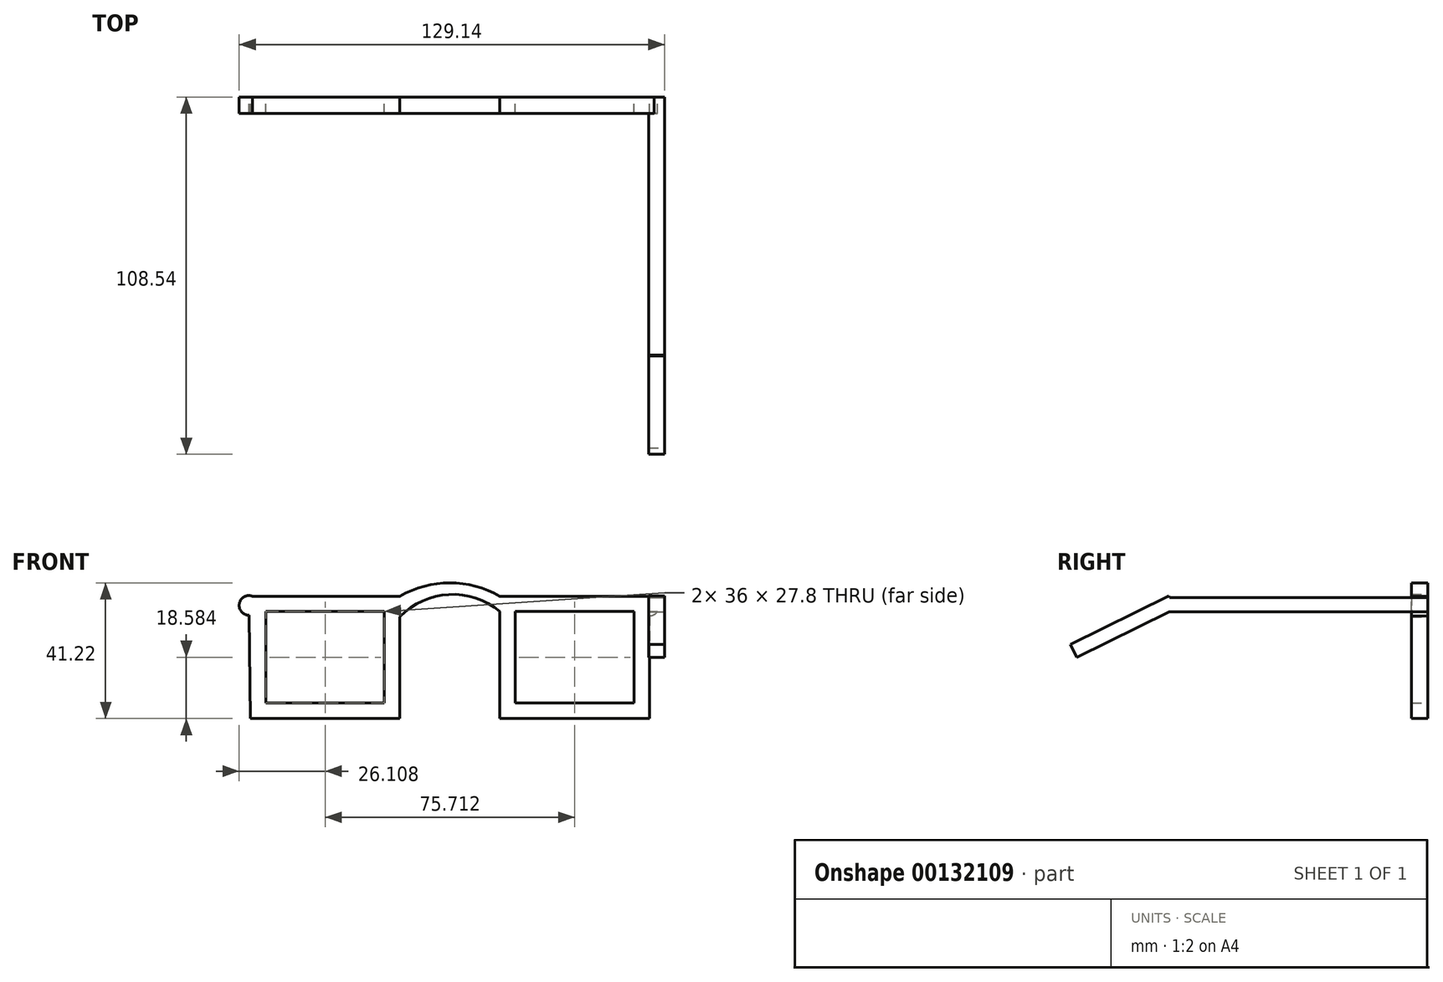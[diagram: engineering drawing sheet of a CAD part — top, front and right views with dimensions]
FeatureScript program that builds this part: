
annotation { "Feature Type Name" : "Feature", "Feature Type Description" : "" }
export const myFeature = defineFeature(function(context is Context, id is Id, definition is map)
    precondition{}
    {
        {
            var Q0;
            Q0=qCreatedBy(makeId("Front.planeOp"),FACE);
            var sketch = newSketch(context, id + "F0", { "sketchPlane" : qUnion([Q0])});
            skLineSegment(sketch, "E0.bottom", {"start": v(-75.72, 32.65) * mm, "end": v(-30.35, 32.65) * mm});
            skLineSegment(sketch, "E0.top", {"start": v(-75.72, -4.5) * mm, "end": v(-30.35, -4.5) * mm});
            skLineSegment(sketch, "E0.right", {"start": v(-30.35, 26.4) * mm, "end": v(-30.35, -4.5) * mm});
            skPoint(sketch, "E0.middle", {"position": v(-53.03, 14.07) * mm});
            skLineSegment(sketch, "E1.bottom", {"start": v(-71.03, 27.97) * mm, "end": v(-35.03, 27.97) * mm});
            skLineSegment(sketch, "E1.top", {"start": v(-71.03, 0.17) * mm, "end": v(-35.03, 0.17) * mm});
            skLineSegment(sketch, "E1.left", {"start": v(-71.03, 27.97) * mm, "end": v(-71.03, 0.17) * mm});
            skLineSegment(sketch, "E1.right", {"start": v(-35.03, 27.97) * mm, "end": v(-35.03, 0.17) * mm});
            skArc(sketch, "E2", {"start": v(-75.13, 32.65) * mm, "mid": v(-79.1, 30.37) * mm, "end": v(-76.16, 26.86) * mm});
            skLineSegment(sketch, "E3.trimOffspring", {"start": v(-76.16, 26.86) * mm, "end": v(-75.72, -4.5) * mm});
            skArc(sketch, "E4", {"start": v(0, 32.65) * mm, "mid": v(-15.17, 36.71) * mm, "end": v(-30.35, 32.65) * mm});
            skArc(sketch, "E5", {"start": v(0, 27.97) * mm, "mid": v(-15.48, 33.16) * mm, "end": v(-30.35, 26.4) * mm});
            skLineSegment(sketch, "E6.bottom", {"start": v(4.68, 27.97) * mm, "end": v(40.68, 27.97) * mm});
            skLineSegment(sketch, "E6.top", {"start": v(4.68, 0.17) * mm, "end": v(40.68, 0.17) * mm});
            skLineSegment(sketch, "E6.left", {"start": v(4.68, 27.97) * mm, "end": v(4.68, 0.17) * mm});
            skLineSegment(sketch, "E6.right", {"start": v(40.68, 27.97) * mm, "end": v(40.68, 0.17) * mm});
            skPoint(sketch, "E6.middle", {"position": v(22.68, 14.07) * mm});
            skLineSegment(sketch, "E7.bottom", {"start": v(0, 32.65) * mm, "end": v(45.36, 32.65) * mm});
            skLineSegment(sketch, "E7.top", {"start": v(0, -4.5) * mm, "end": v(45.36, -4.5) * mm});
            skLineSegment(sketch, "E7.left", {"start": v(0, 32.65) * mm, "end": v(0, -4.5) * mm});
            skArc(sketch, "E8", {"start": v(45.36, 26.67) * mm, "mid": v(48.35, 29.66) * mm, "end": v(45.36, 32.65) * mm});
            skLineSegment(sketch, "E9.trimOffspring", {"start": v(45.36, 26.67) * mm, "end": v(45.36, -4.5) * mm});
            skSolve(sketch);
        }
        {
            var Q0;
            Q0 = qSketchRegion(id + "F0", true);
            extrude(context, id + "F1", {"entities" : qUnion([Q0]), "depth" : 5 * mm});
        }
        {
            var Q0;
            Q0=qCreatedBy(makeId("Right.planeOp"),FACE);
            cPlane(context, id + "F2", {"entities" : qUnion([Q0]), "cplaneType" : CPlaneType.OFFSET, "offset" : 50 * mm, "width" : 150 * mm, "height" : 150 * mm});
        }
        {
            var Q0;
            Q0=qCreatedBy(id+"F2.planeOp",FACE);
            var sketch = newSketch(context, id + "F3", { "sketchPlane" : qUnion([Q0])});
            skLineSegment(sketch, "E10.bottom", {"start": v(0, 32.25) * mm, "end": v(-78.97, 32.25) * mm});
            skLineSegment(sketch, "E10.top", {"start": v(0, 27.92) * mm, "end": v(-78.97, 27.92) * mm});
            skLineSegment(sketch, "E10.left", {"start": v(0, 32.25) * mm, "end": v(0, 27.92) * mm});
            skLineSegment(sketch, "E11.bottom", {"start": v(-78.61, 32.72) * mm, "end": v(-108.54, 17.93) * mm});
            skLineSegment(sketch, "E11.top", {"start": v(-78.54, 27.92) * mm, "end": v(-106.62, 14.05) * mm});
            skLineSegment(sketch, "E11.left", {"start": v(-78.61, 32.72) * mm, "end": v(-78.38, 32.25) * mm});
            skLineSegment(sketch, "E11.right", {"start": v(-108.54, 17.93) * mm, "end": v(-106.62, 14.05) * mm});
            skSolve(sketch);
        }
        {
            var Q0;
            Q0 = qSketchRegion(id + "F3", true);
            var Q1;
            Q1=makeQuery(id+"F1.opExtrude","SWEPT_BODY",BODY,{"disambiguationData":[OSD([sQuery(id+"F0.wireOp",EDGE,"E0.bottom"),sQuery(id+"F0.wireOp",EDGE,"E0.top"),sQuery(id+"F0.wireOp",EDGE,"E0.right"),sQuery(id+"F0.wireOp",EDGE,"E1.bottom"),sQuery(id+"F0.wireOp",EDGE,"E1.top"),sQuery(id+"F0.wireOp",EDGE,"E1.left"),sQuery(id+"F0.wireOp",EDGE,"E1.right"),sQuery(id+"F0.wireOp",EDGE,"E2"),sQuery(id+"F0.wireOp",EDGE,"E3.trimOffspring"),sQuery(id+"F0.wireOp",EDGE,"E4"),sQuery(id+"F0.wireOp",EDGE,"E5"),sQuery(id+"F0.wireOp",EDGE,"E6.bottom"),sQuery(id+"F0.wireOp",EDGE,"E6.top"),sQuery(id+"F0.wireOp",EDGE,"E6.left"),sQuery(id+"F0.wireOp",EDGE,"E6.right"),sQuery(id+"F0.wireOp",EDGE,"E7.bottom"),sQuery(id+"F0.wireOp",EDGE,"E7.top"),sQuery(id+"F0.wireOp",EDGE,"E7.left"),sQuery(id+"F0.wireOp",EDGE,"E8"),sQuery(id+"F0.wireOp",EDGE,"E9.trimOffspring")])]});
            extrude(context, id + "F4", {"entities" : qUnion([Q0]), "operationType" : NewBodyOperationType.ADD, "oppositeDirection" : true, "endBoundEntityBody" : qUnion([Q1]), "depth" : 4.9 * mm});
        }
    });
